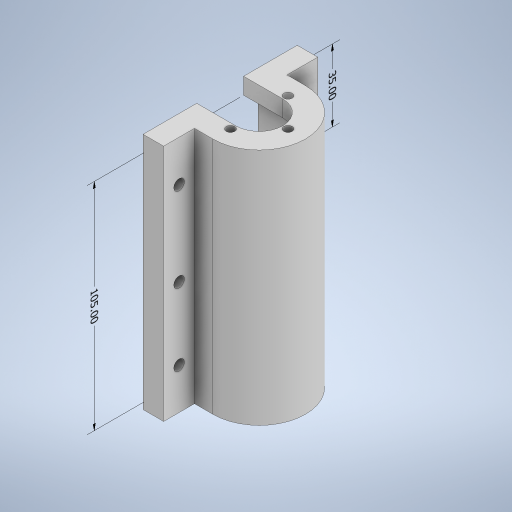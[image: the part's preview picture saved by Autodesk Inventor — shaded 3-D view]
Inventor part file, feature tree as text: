
AUTODESK INVENTOR PART (.ipt)
format: ipt  version: 2023 (Build 270158000, 158)  size: 350,208 bytes
history: native  units: mm
features: extrude x6, sketch x6, other x4
ambient origin geometry x8: Origin, YZ Plane, XZ Plane, XY Plane, X Axis, Y Axis, Z Axis, Center Point
bodies: Body1 (feature_tree)
feature tree (16):
  other  "Sólido1"
  other  "Anotaciones"
  extrude  "Extrusión1"  Depth=4.2mm
  extrude  "Extrusión2"  Depth=8.0mm TaperAngle=0.0deg
  extrude  "Extrusión3"  Depth=11.4mm
  extrude  "Extrusión4"  Depth=8.0mm TaperAngle=0.0deg
  extrude  "Extrusión5"  Depth=38.0mm
  extrude  "Extrusión6"  Depth=3.0mm TaperAngle=0.0deg
  sketch  "Boceto1"  dims[d0=28.0mm d1=4.2mm]
  sketch  "Boceto2"  dims[d3=22.0mm d7=8.0mm d8=0.0mm]
  sketch  "Boceto3"  dims[d10=35.0mm d11=0.0mm d12=11.4mm]
  sketch  "Boceto4"  dims[d14=37.0mm d16=8.0mm d17=0.0mm]
  sketch  "Boceto5"  dims[d18=4.2mm d19=38.0mm]
  sketch  "Boceto6"  dims[d21=70.0mm d22=0.0mm d23=3.0mm d24=0.0mm d25=15.0mm d26=5.2mm d27=5.2mm d28=20.0mm d30=10.0mm d31=0.0mm d32=7.915891mm d33=5.339445mm d34=35.0mm d35=6.253949mm d36=8.66829mm d37=105.0mm]
  other  "Cota lineal 1"
  other  "Cota lineal 2"
